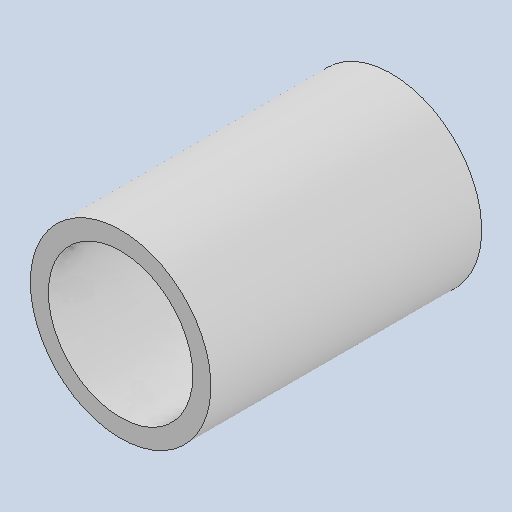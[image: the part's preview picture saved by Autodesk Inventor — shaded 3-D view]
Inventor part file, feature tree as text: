
AUTODESK INVENTOR PART (.ipt)
format: ipt  version: 2023 (Build 270158030, 158C)  size: 108,032 bytes
history: native  units: in
note: dims shown in document units (in); Inventor stores cm internally (conversion verified against a paired STEP export)
features: extrude x1
ambient origin geometry x8: Origin, YZ Plane, XZ Plane, XY Plane, X Axis, Y Axis, Z Axis, Center Point
bodies: Solid1 (feature_tree)
feature tree (1):
  extrude  "Extrude1"  [1 undecoded]
note: 1 required parameter value undecoded (feature->parameter linkage not recoverable at this tier; creation-order binding heuristic only, values carry confidence <= 0.55)
